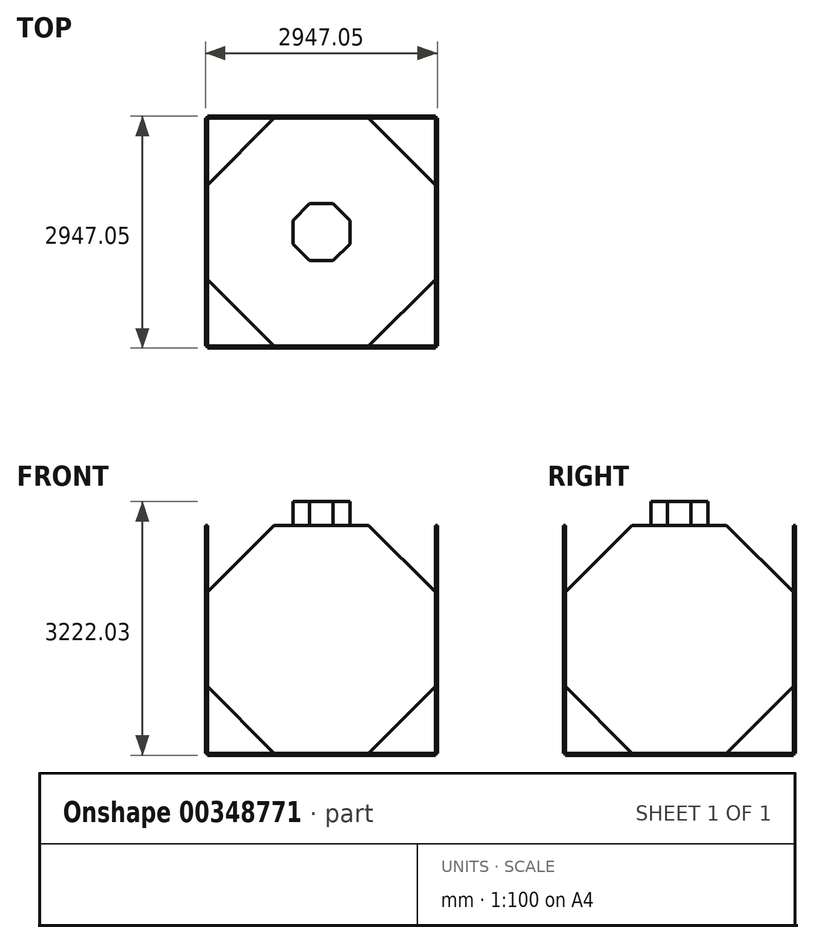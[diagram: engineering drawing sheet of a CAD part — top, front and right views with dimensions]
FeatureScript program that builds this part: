
annotation { "Feature Type Name" : "Feature", "Feature Type Description" : "" }
export const myFeature = defineFeature(function(context is Context, id is Id, definition is map)
    precondition{}
    {
        {
            var Q0;
            Q0=qCreatedBy(makeId("Top.planeOp"),FACE);
            var sketch = newSketch(context, id + "F0", { "sketchPlane" : qUnion([Q0])});
            skCircle(sketch, "E0.cCircle", {"center": v(-783.25, 1024.26) * mm, "radius": 1448.53 * mm, "construction": true});
            skLineSegment(sketch, "E0.0", {"start": v(665.28, 424.26) * mm, "end": v(-183.25, -424.26) * mm});
            skLineSegment(sketch, "E0.1", {"start": v(-183.25, -424.26) * mm, "end": v(-1383.25, -424.26) * mm});
            skLineSegment(sketch, "E0.2", {"start": v(-1383.25, -424.26) * mm, "end": v(-2231.77, 424.26) * mm});
            skLineSegment(sketch, "E0.3", {"start": v(-2231.77, 424.26) * mm, "end": v(-2231.77, 1624.26) * mm});
            skLineSegment(sketch, "E0.4", {"start": v(-2231.77, 1624.26) * mm, "end": v(-1383.25, 2472.8) * mm});
            skLineSegment(sketch, "E0.5", {"start": v(-1383.25, 2472.8) * mm, "end": v(-183.25, 2472.8) * mm});
            skLineSegment(sketch, "E0.6", {"start": v(-183.25, 2472.8) * mm, "end": v(665.28, 1624.26) * mm});
            skLineSegment(sketch, "E0.7", {"start": v(665.28, 1624.26) * mm, "end": v(665.28, 424.26) * mm});
            skPoint(sketch, "E0.0.midPoint", {"position": v(241.02, 0) * mm});
            skLineSegment(sketch, "E1", {"start": v(-2231.77, 1024.26) * mm, "end": v(665.28, 1024.26) * mm, "construction": true});
            skSolve(sketch);
        }
        {
            var Q0;
            Q0=makeQuery(id+"F0.imprint","IMPRINT",FACE,{"disambiguationData":[TD([[makeQuery(id+"F0.imprint","IMPRINT",EDGE,{"derivedFrom":sQuery(id+"F0.wireOp",EDGE,"E0.0")}),-1.0]])]});
            extrude(context, id + "F1", {"entities" : qUnion([Q0]), "depth" : 25 * mm});
        }
        {
            var Q0;
            Q0=makeQuery(id+"F1.opExtrude","SWEPT_FACE",FACE,{"disambiguationData":[OSD([sQuery(id+"F0.wireOp",EDGE,"E0.1")])]});
            var sketch = newSketch(context, id + "F2", { "sketchPlane" : qUnion([Q0])});
            skLineSegment(sketch, "E2", {"start": v(-783.25, 25) * mm, "end": v(-783.25, 1473.5) * mm, "construction": true});
            skCircle(sketch, "E3.cCircle", {"center": v(-783.25, 1473.5) * mm, "radius": 1448.53 * mm, "construction": true});
            skLineSegment(sketch, "E3.0", {"start": v(-183.25, 24.97) * mm, "end": v(-1383.25, 24.97) * mm});
            skLineSegment(sketch, "E3.1", {"start": v(-1383.25, 24.97) * mm, "end": v(-2231.77, 873.5) * mm});
            skLineSegment(sketch, "E3.2", {"start": v(-2231.77, 873.5) * mm, "end": v(-2231.77, 2073.5) * mm});
            skLineSegment(sketch, "E3.3", {"start": v(-2231.77, 2073.5) * mm, "end": v(-1383.25, 2922.03) * mm});
            skLineSegment(sketch, "E3.4", {"start": v(-1383.25, 2922.03) * mm, "end": v(-183.25, 2922.03) * mm});
            skLineSegment(sketch, "E3.5", {"start": v(-183.25, 2922.03) * mm, "end": v(665.28, 2073.5) * mm});
            skLineSegment(sketch, "E3.6", {"start": v(665.28, 2073.5) * mm, "end": v(665.28, 873.5) * mm});
            skLineSegment(sketch, "E3.7", {"start": v(665.28, 873.5) * mm, "end": v(-183.25, 24.97) * mm});
            skPoint(sketch, "E3.0.midPoint", {"position": v(-783.25, 24.97) * mm});
            skSolve(sketch);
        }
        {
            var Q0;
            {var subQ3=sQuery(id+"F2.wireOp",EDGE,"E3.1");Q0=makeQuery(id+"F2.imprint","IMPRINT",FACE,{"disambiguationData":[TD([[makeQuery(id+"F2.imprint","IMPRINT",EDGE,{"derivedFrom":subQ3}),-1.0]])]});}
            extrude(context, id + "F3", {"entities" : qUnion([Q0]), "depth" : 25 * mm});
        }
        {
            var Q0;
            Q0=makeQuery(id+"F1.opExtrude","SWEPT_FACE",FACE,{"disambiguationData":[OSD([sQuery(id+"F0.wireOp",EDGE,"E0.5")])]});
            var sketch = newSketch(context, id + "F4", { "sketchPlane" : qUnion([Q0])});
            skLineSegment(sketch, "E4", {"start": v(783.25, 25) * mm, "end": v(783.25, 1473.5) * mm, "construction": true});
            skCircle(sketch, "E5.cCircle", {"center": v(783.25, 1473.5) * mm, "radius": 1448.53 * mm, "construction": true});
            skLineSegment(sketch, "E5.0", {"start": v(2231.77, 873.5) * mm, "end": v(1383.25, 24.97) * mm});
            skLineSegment(sketch, "E5.1", {"start": v(1383.25, 24.97) * mm, "end": v(183.25, 24.97) * mm});
            skLineSegment(sketch, "E5.2", {"start": v(183.25, 24.97) * mm, "end": v(-665.28, 873.5) * mm});
            skLineSegment(sketch, "E5.3", {"start": v(-665.28, 873.5) * mm, "end": v(-665.28, 2073.5) * mm});
            skLineSegment(sketch, "E5.4", {"start": v(-665.28, 2073.5) * mm, "end": v(183.25, 2922.03) * mm});
            skLineSegment(sketch, "E5.5", {"start": v(183.25, 2922.03) * mm, "end": v(1383.25, 2922.03) * mm});
            skLineSegment(sketch, "E5.6", {"start": v(1383.25, 2922.03) * mm, "end": v(2231.77, 2073.5) * mm});
            skLineSegment(sketch, "E5.7", {"start": v(2231.77, 2073.5) * mm, "end": v(2231.77, 873.5) * mm});
            skPoint(sketch, "E5.0.midPoint", {"position": v(1807.51, 449.24) * mm});
            skSolve(sketch);
        }
        {
            var Q0;
            {var subQ5=sQuery(id+"F4.wireOp",EDGE,"E5.0");Q0=makeQuery(id+"F4.imprint","IMPRINT",FACE,{"disambiguationData":[TD([[makeQuery(id+"F4.imprint","IMPRINT",EDGE,{"derivedFrom":subQ5}),-1.0]])]});}
            extrude(context, id + "F5", {"entities" : qUnion([Q0]), "depth" : 25 * mm});
        }
        {
            var Q0;
            Q0=makeQuery(id+"F1.opExtrude","SWEPT_FACE",FACE,{"disambiguationData":[OSD([sQuery(id+"F0.wireOp",EDGE,"E0.7")])]});
            var sketch = newSketch(context, id + "F6", { "sketchPlane" : qUnion([Q0])});
            skLineSegment(sketch, "E6", {"start": v(1024.26, 25) * mm, "end": v(1024.26, 1473.5) * mm, "construction": true});
            skPoint(sketch, "E6.endSnap0", {"position": v(1024.26, 25) * mm});
            skCircle(sketch, "E7.cCircle", {"center": v(1024.26, 1473.5) * mm, "radius": 1448.53 * mm, "construction": true});
            skLineSegment(sketch, "E7.0", {"start": v(1624.26, 24.97) * mm, "end": v(424.26, 24.97) * mm});
            skLineSegment(sketch, "E7.1", {"start": v(424.26, 24.97) * mm, "end": v(-424.26, 873.5) * mm});
            skLineSegment(sketch, "E7.2", {"start": v(-424.26, 873.5) * mm, "end": v(-424.26, 2073.5) * mm});
            skLineSegment(sketch, "E7.3", {"start": v(-424.26, 2073.5) * mm, "end": v(424.26, 2922.03) * mm});
            skLineSegment(sketch, "E7.4", {"start": v(424.26, 2922.03) * mm, "end": v(1624.26, 2922.03) * mm});
            skLineSegment(sketch, "E7.5", {"start": v(1624.26, 2922.03) * mm, "end": v(2472.8, 2073.5) * mm});
            skLineSegment(sketch, "E7.6", {"start": v(2472.8, 2073.5) * mm, "end": v(2472.8, 873.5) * mm});
            skLineSegment(sketch, "E7.7", {"start": v(2472.8, 873.5) * mm, "end": v(1624.26, 24.97) * mm});
            skPoint(sketch, "E7.0.midPoint", {"position": v(1024.26, 24.97) * mm});
            skSolve(sketch);
        }
        {
            var Q0;
            {var subQ5=sQuery(id+"F6.wireOp",EDGE,"E7.1");Q0=makeQuery(id+"F6.imprint","IMPRINT",FACE,{"disambiguationData":[TD([[makeQuery(id+"F6.imprint","IMPRINT",EDGE,{"derivedFrom":subQ5}),-1.0]])]});}
            extrude(context, id + "F7", {"entities" : qUnion([Q0]), "depth" : 25 * mm});
        }
        {
            var Q0;
            Q0=makeQuery(id+"F1.opExtrude","SWEPT_FACE",FACE,{"disambiguationData":[OSD([sQuery(id+"F0.wireOp",EDGE,"E0.3")])]});
            var sketch = newSketch(context, id + "F8", { "sketchPlane" : qUnion([Q0])});
            skLineSegment(sketch, "E8", {"start": v(-1024.26, 25) * mm, "end": v(-1024.26, 1473.5) * mm, "construction": true});
            skCircle(sketch, "E9.cCircle", {"center": v(-1024.26, 1473.5) * mm, "radius": 1448.53 * mm, "construction": true});
            skLineSegment(sketch, "E9.0", {"start": v(-424.26, 24.97) * mm, "end": v(-1624.26, 24.97) * mm});
            skLineSegment(sketch, "E9.1", {"start": v(-1624.26, 24.97) * mm, "end": v(-2472.8, 873.5) * mm});
            skLineSegment(sketch, "E9.2", {"start": v(-2472.8, 873.5) * mm, "end": v(-2472.8, 2073.5) * mm});
            skLineSegment(sketch, "E9.3", {"start": v(-2472.8, 2073.5) * mm, "end": v(-1624.26, 2922.03) * mm});
            skLineSegment(sketch, "E9.4", {"start": v(-1624.26, 2922.03) * mm, "end": v(-424.26, 2922.03) * mm});
            skLineSegment(sketch, "E9.5", {"start": v(-424.26, 2922.03) * mm, "end": v(424.26, 2073.5) * mm});
            skLineSegment(sketch, "E9.6", {"start": v(424.26, 2073.5) * mm, "end": v(424.26, 873.5) * mm});
            skLineSegment(sketch, "E9.7", {"start": v(424.26, 873.5) * mm, "end": v(-424.26, 24.97) * mm});
            skPoint(sketch, "E9.0.midPoint", {"position": v(-1024.26, 24.97) * mm});
            skSolve(sketch);
        }
        {
            var Q0;
            {var subQ3=sQuery(id+"F8.wireOp",EDGE,"E9.1");Q0=makeQuery(id+"F8.imprint","IMPRINT",FACE,{"disambiguationData":[TD([[makeQuery(id+"F8.imprint","IMPRINT",EDGE,{"derivedFrom":subQ3}),-1.0]])]});}
            extrude(context, id + "F9", {"entities" : qUnion([Q0]), "depth" : 25 * mm});
        }
        {
            var Q0;
            Q0=makeQuery(id+"F3.opExtrude","SWEPT_FACE",FACE,{"disambiguationData":[OSD([sQuery(id+"F2.wireOp",EDGE,"E3.4")])]});
            var sketch = newSketch(context, id + "F10", { "sketchPlane" : qUnion([Q0])});
            skLineSegment(sketch, "E10", {"start": v(-783.25, -424.26) * mm, "end": v(-783.25, 2471.04) * mm, "construction": true});
            skLineSegment(sketch, "E11", {"start": v(-783.25, 1023.39) * mm, "end": v(670.18, 1023.39) * mm, "construction": true});
            skPoint(sketch, "E11.endSnap0", {"position": v(-783.25, 1023.39) * mm});
            skLineSegment(sketch, "E12", {"start": v(-783.25, 1023.39) * mm, "end": v(-2225.7, 1023.39) * mm, "construction": true});
            skCircle(sketch, "E13.cCircle", {"center": v(-783.25, 1023.39) * mm, "radius": 362.13 * mm, "construction": true});
            skLineSegment(sketch, "E13.0", {"start": v(-633.25, 661.26) * mm, "end": v(-933.25, 661.26) * mm});
            skLineSegment(sketch, "E13.1", {"start": v(-933.25, 661.26) * mm, "end": v(-1145.38, 873.39) * mm});
            skLineSegment(sketch, "E13.2", {"start": v(-1145.38, 873.39) * mm, "end": v(-1145.38, 1173.39) * mm});
            skLineSegment(sketch, "E13.3", {"start": v(-1145.38, 1173.39) * mm, "end": v(-933.25, 1385.52) * mm});
            skLineSegment(sketch, "E13.4", {"start": v(-933.25, 1385.52) * mm, "end": v(-633.25, 1385.52) * mm});
            skLineSegment(sketch, "E13.5", {"start": v(-633.25, 1385.52) * mm, "end": v(-421.11, 1173.39) * mm});
            skLineSegment(sketch, "E13.6", {"start": v(-421.11, 1173.39) * mm, "end": v(-421.11, 873.39) * mm});
            skLineSegment(sketch, "E13.7", {"start": v(-421.11, 873.39) * mm, "end": v(-633.25, 661.26) * mm});
            skPoint(sketch, "E13.0.midPoint", {"position": v(-783.25, 661.26) * mm});
            skCircle(sketch, "E14.cCircle", {"center": v(-783.25, 1023.39) * mm, "radius": 1448.53 * mm, "construction": true});
            skLineSegment(sketch, "E14.0", {"start": v(665.28, 423.39) * mm, "end": v(-183.25, -425.14) * mm});
            skLineSegment(sketch, "E14.1", {"start": v(-183.25, -425.14) * mm, "end": v(-1383.25, -425.14) * mm});
            skLineSegment(sketch, "E14.2", {"start": v(-1383.25, -425.14) * mm, "end": v(-2231.77, 423.39) * mm});
            skLineSegment(sketch, "E14.3", {"start": v(-2231.77, 423.39) * mm, "end": v(-2231.77, 1623.39) * mm});
            skLineSegment(sketch, "E14.4", {"start": v(-2231.77, 1623.39) * mm, "end": v(-1383.25, 2471.92) * mm});
            skLineSegment(sketch, "E14.5", {"start": v(-1383.25, 2471.92) * mm, "end": v(-183.25, 2471.92) * mm});
            skLineSegment(sketch, "E14.6", {"start": v(-183.25, 2471.92) * mm, "end": v(665.28, 1623.39) * mm});
            skLineSegment(sketch, "E14.7", {"start": v(665.28, 1623.39) * mm, "end": v(665.28, 423.39) * mm});
            skPoint(sketch, "E14.0.midPoint", {"position": v(241.02, -0.88) * mm});
            skSolve(sketch);
        }
        {
            var Q0;
            Q0=makeQuery(id+"F10.imprint","IMPRINT",FACE,{"disambiguationData":[TD([[makeQuery(id+"F10.imprint","IMPRINT",EDGE,{"derivedFrom":sQuery(id+"F10.wireOp",EDGE,"E13.0")}),-1.0]])]});
            extrude(context, id + "F11", {"entities" : qUnion([Q0]), "depth" : 300 * mm});
        }
    });
